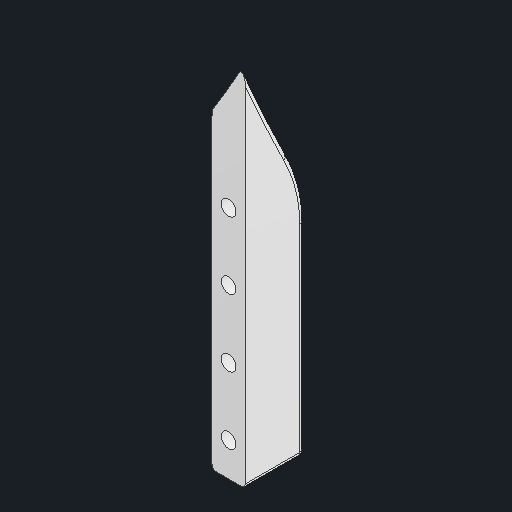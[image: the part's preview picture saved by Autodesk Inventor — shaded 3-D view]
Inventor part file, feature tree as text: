
AUTODESK INVENTOR PART (.ipt)
format: ipt  version: 2024.3 (Build 283343010, 343A)  size: 144,384 bytes
history: native  units: in
note: dims shown in document units (in); Inventor stores cm internally (conversion verified against a paired STEP export)
features: other x3, sketch x2
ambient origin geometry x8: Origin, YZ Plane, XZ Plane, XY Plane, X Axis, Y Axis, Z Axis, Center Point
bodies: Solid1 (feature_tree)
feature tree (5):
  other  "coral_guide.ipt"
  other  "Solid1::coral_guide.ipt"
  other  "TaggingFeature1"
  sketch  "Sketch1"  dims[d0=0.3937in]
  sketch  "Sketch2"
